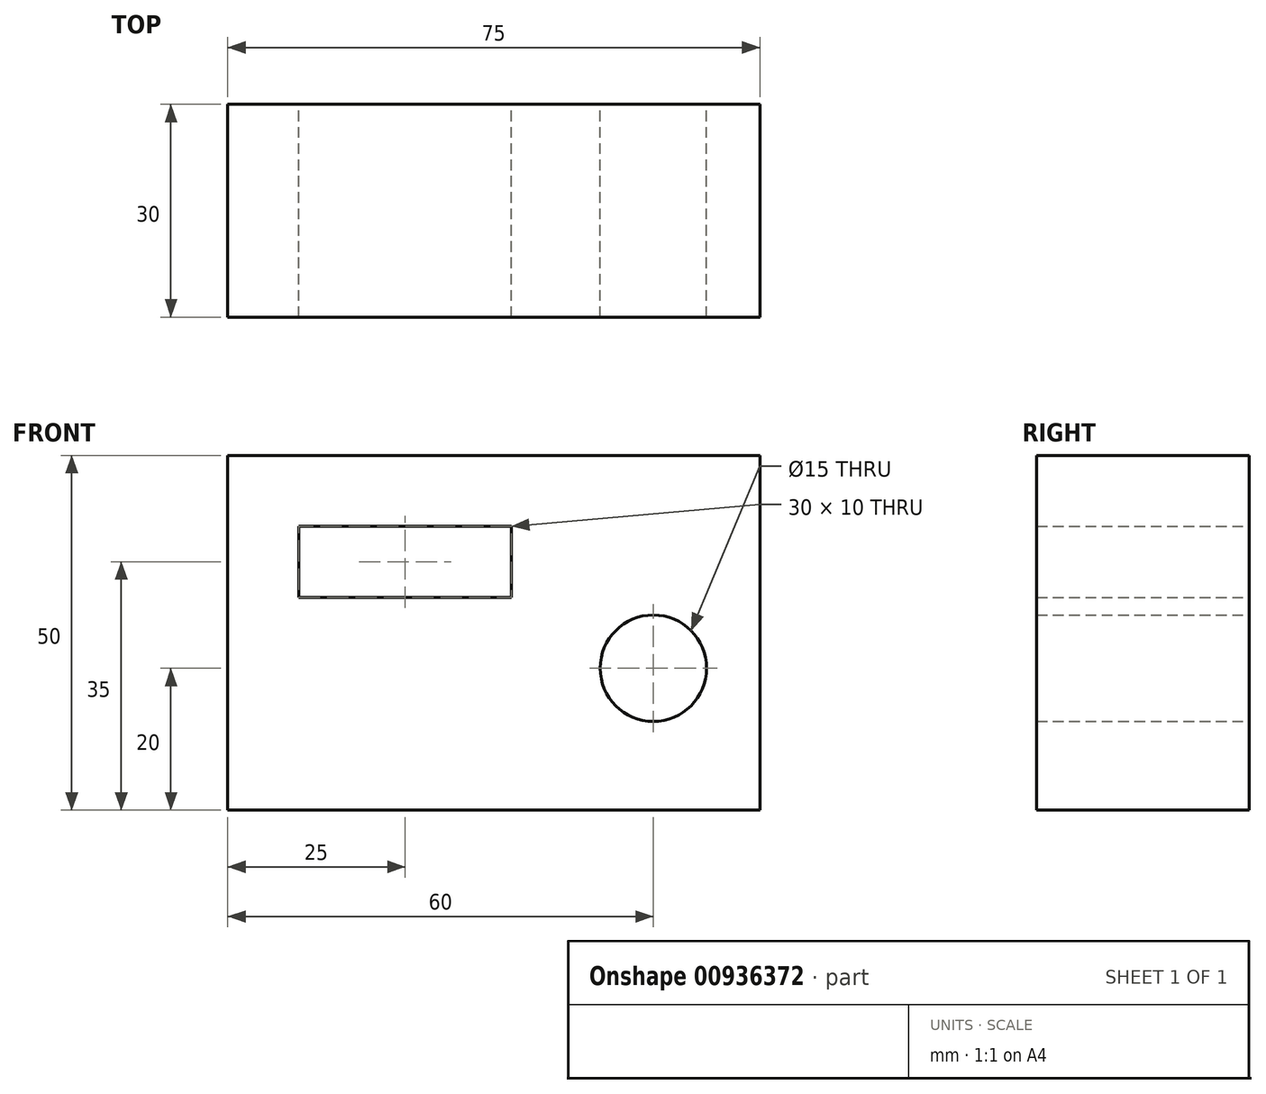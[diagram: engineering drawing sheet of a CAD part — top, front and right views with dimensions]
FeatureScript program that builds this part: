
annotation { "Feature Type Name" : "Feature", "Feature Type Description" : "" }
export const myFeature = defineFeature(function(context is Context, id is Id, definition is map)
    precondition{}
    {
        {
            var Q0;
            Q0=qCreatedBy(makeId("Front.planeOp"),FACE);
            var sketch = newSketch(context, id + "F0", { "sketchPlane" : qUnion([Q0])});
            skLineSegment(sketch, "E0", {"start": v(0, 0) * mm, "end": v(15, 0) * mm});
            skLineSegment(sketch, "E1", {"start": v(15, 0) * mm, "end": v(15, -20) * mm});
            skLineSegment(sketch, "E2", {"start": v(15, -20) * mm, "end": v(0, -20) * mm});
            skLineSegment(sketch, "E3", {"start": v(0, -20) * mm, "end": v(0, 0) * mm});
            skLineSegment(sketch, "E4", {"start": v(0, -20) * mm, "end": v(-60, -20) * mm});
            skLineSegment(sketch, "E5", {"start": v(-60, -20) * mm, "end": v(-60, 30) * mm});
            skLineSegment(sketch, "E6", {"start": v(-60, 30) * mm, "end": v(15, 30) * mm});
            skLineSegment(sketch, "E7", {"start": v(15, 30) * mm, "end": v(15, 0) * mm});
            skCircle(sketch, "E8", {"center": v(0, 0) * mm, "radius": 7.5 * mm});
            skLineSegment(sketch, "E9", {"start": v(-50, 30) * mm, "end": v(-50, 20) * mm});
            skLineSegment(sketch, "E10", {"start": v(-50, 20) * mm, "end": v(-60, 20) * mm});
            skLineSegment(sketch, "E11", {"start": v(-50, 20) * mm, "end": v(-20, 20) * mm});
            skLineSegment(sketch, "E12", {"start": v(-20, 20) * mm, "end": v(-20, 10) * mm});
            skLineSegment(sketch, "E13", {"start": v(-20, 10) * mm, "end": v(-50, 10) * mm});
            skLineSegment(sketch, "E14", {"start": v(-50, 10) * mm, "end": v(-50, 20) * mm});
            skSolve(sketch);
        }
        {
            var Q0;
            {var subQ4=sQuery(id+"F0.wireOp",EDGE,"E9");Q0=makeQuery(id+"F0.imprint","IMPRINT",FACE,{"disambiguationData":[TD([[makeQuery(id+"F0.imprint","IMPRINT",EDGE,{"derivedFrom":subQ4}),-1.0]])]});}
            var Q1;
            {var subQ4=sQuery(id+"F0.wireOp",EDGE,"E1");Q1=makeQuery(id+"F0.imprint","IMPRINT",FACE,{"disambiguationData":[TD([[makeQuery(id+"F0.imprint","IMPRINT",EDGE,{"derivedFrom":subQ4}),-1.0]])]});}
            var Q2;
            {var subQ8=sQuery(id+"F0.wireOp",EDGE,"E4");Q2=makeQuery(id+"F0.imprint","IMPRINT",FACE,{"disambiguationData":[TD([[makeQuery(id+"F0.imprint","IMPRINT",EDGE,{"derivedFrom":subQ8}),-1.0]])]});}
            extrude(context, id + "F1", {"entities" : qUnion([Q0, Q1, Q2]), "depth" : 30 * mm, "offsetDistance" : 25 * mm});
        }
    });
